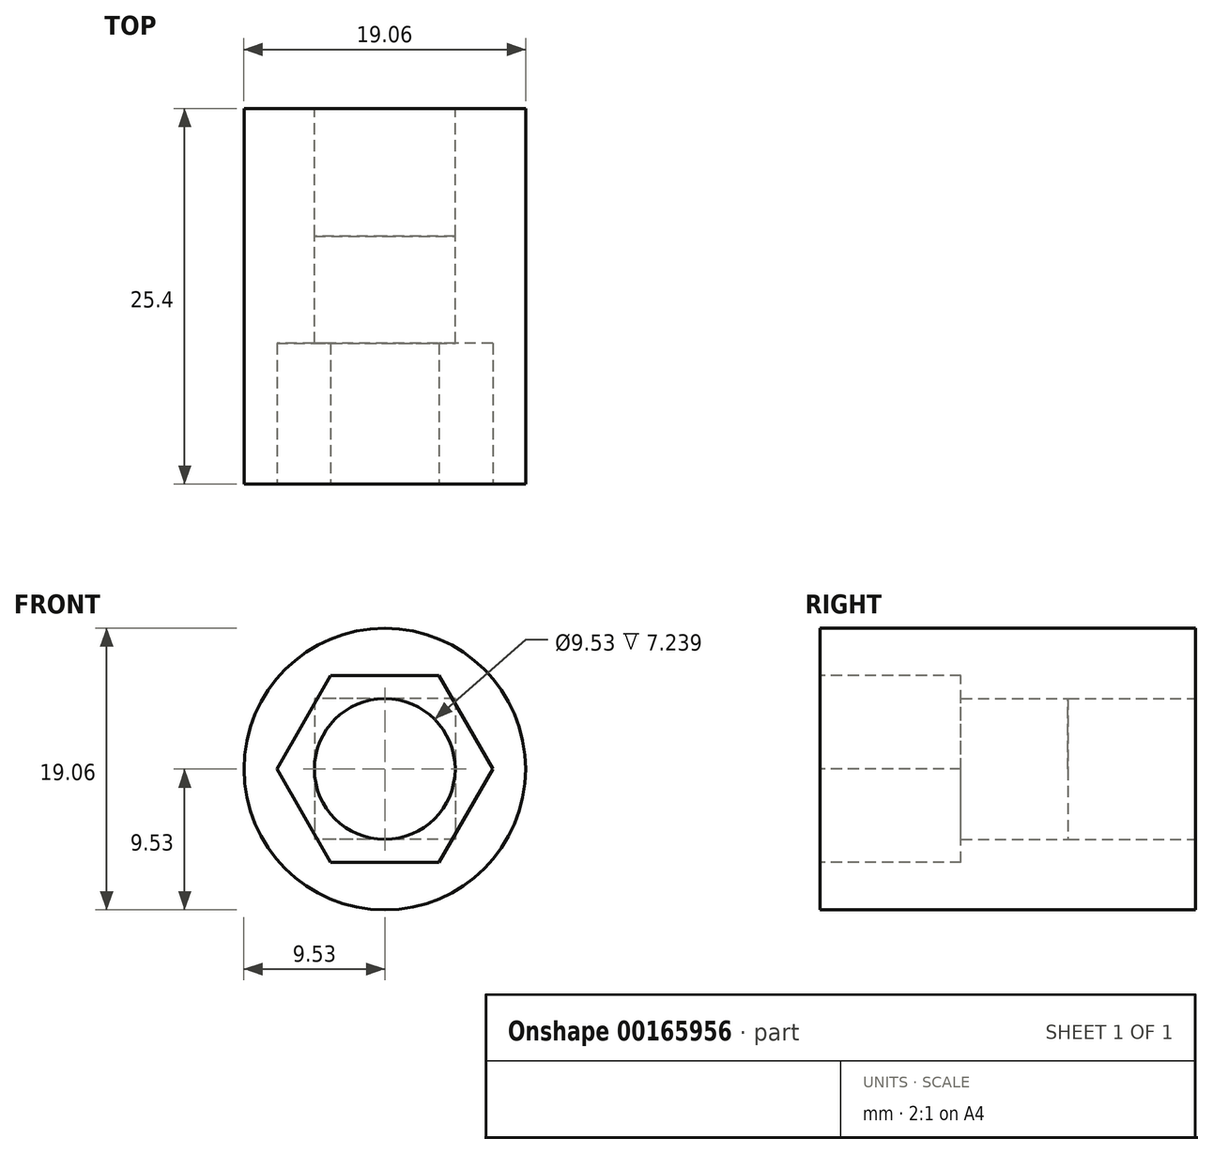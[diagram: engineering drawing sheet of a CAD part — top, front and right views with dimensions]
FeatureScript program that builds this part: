
annotation { "Feature Type Name" : "Feature", "Feature Type Description" : "" }
export const myFeature = defineFeature(function(context is Context, id is Id, definition is map)
    precondition{}
    {
        {
            var Q0;
            Q0=qCreatedBy(makeId("Front.planeOp"),FACE);
            var sketch = newSketch(context, id + "F0", { "sketchPlane" : qUnion([Q0])});
            skCircle(sketch, "E0", {"center": v(0, 0) * mm, "radius": 9.53 * mm});
            skSolve(sketch);
        }
        {
            var Q0;
            Q0 = qSketchRegion(id + "F0", true);
            extrude(context, id + "F1", {"entities" : qUnion([Q0]), "depth" : 25.4 * mm});
        }
        {
            var Q0;
            Q0=qCreatedBy(makeId("Front.planeOp"),FACE);
            var sketch = newSketch(context, id + "F2", { "sketchPlane" : qUnion([Q0])});
            skLineSegment(sketch, "E1.bottom", {"start": v(4.76, 4.76) * mm, "end": v(-4.76, 4.76) * mm});
            skLineSegment(sketch, "E1.top", {"start": v(4.76, -4.76) * mm, "end": v(-4.76, -4.76) * mm});
            skLineSegment(sketch, "E1.left", {"start": v(4.76, 4.76) * mm, "end": v(4.76, -4.76) * mm});
            skLineSegment(sketch, "E1.right", {"start": v(-4.76, 4.76) * mm, "end": v(-4.76, -4.76) * mm});
            skPoint(sketch, "E1.middle", {"position": v(0, 0) * mm});
            skPoint(sketch, "E2.middle", {"position": v(-4.76, 1.68) * mm});
            skCircle(sketch, "E3", {"center": v(0, 0) * mm, "radius": 4.76 * mm});
            skSolve(sketch);
        }
        {
            var Q0;
            {var subQ0=sQuery(id+"F2.wireOp",EDGE,"E3");var subQ1=makeQuery(id+"F2.imprint","INTERSECT",VERTEX,{"derivedFrom":[sQuery(id+"F2.wireOp",EDGE,"E1.bottom"),subQ0]});Q0=makeQuery(id+"F2.imprint","IMPRINT",FACE,{"disambiguationData":[TD([[makeQuery(id+"F2.imprint","IMPRINT",EDGE,{"disambiguationData":[TD([[subQ1,1.0]])],"derivedFrom":subQ0}),1.0]])]});}
            extrude(context, id + "F3", {"entities" : qUnion([Q0]), "operationType" : NewBodyOperationType.REMOVE, "endBound" : BoundingType.THROUGH_ALL, "depth" : 25.4 * mm});
        }
        {
            var Q0;
            {var subQ0=sQuery(id+"F2.wireOp",EDGE,"E1.right");var subQ1=sQuery(id+"F2.wireOp",EDGE,"E1.bottom");var subQ2=makeQuery(id+"F2.imprint","INTERSECT",VERTEX,{"derivedFrom":[subQ1,subQ0]});Q0=makeQuery(id+"F2.imprint","IMPRINT",FACE,{"disambiguationData":[TD([[makeQuery(id+"F2.imprint","IMPRINT",EDGE,{"disambiguationData":[TD([[subQ2,1.0]])],"derivedFrom":subQ1}),1.0]])]});}
            var Q1;
            {var subQ0=sQuery(id+"F2.wireOp",EDGE,"E1.left");var subQ1=sQuery(id+"F2.wireOp",EDGE,"E1.bottom");var subQ2=makeQuery(id+"F2.imprint","INTERSECT",VERTEX,{"derivedFrom":[subQ1,subQ0]});Q1=makeQuery(id+"F2.imprint","IMPRINT",FACE,{"disambiguationData":[TD([[makeQuery(id+"F2.imprint","IMPRINT",EDGE,{"disambiguationData":[TD([[subQ2,-1.0]])],"derivedFrom":subQ1}),1.0]])]});}
            var Q2;
            {var subQ0=sQuery(id+"F2.wireOp",EDGE,"E1.right");var subQ1=sQuery(id+"F2.wireOp",EDGE,"E1.top");var subQ2=makeQuery(id+"F2.imprint","INTERSECT",VERTEX,{"derivedFrom":[subQ1,subQ0]});Q2=makeQuery(id+"F2.imprint","IMPRINT",FACE,{"disambiguationData":[TD([[makeQuery(id+"F2.imprint","IMPRINT",EDGE,{"disambiguationData":[TD([[subQ2,1.0]])],"derivedFrom":subQ1}),-1.0]])]});}
            var Q3;
            {var subQ0=sQuery(id+"F2.wireOp",EDGE,"E1.left");var subQ1=sQuery(id+"F2.wireOp",EDGE,"E1.top");var subQ2=makeQuery(id+"F2.imprint","INTERSECT",VERTEX,{"derivedFrom":[subQ1,subQ0]});Q3=makeQuery(id+"F2.imprint","IMPRINT",FACE,{"disambiguationData":[TD([[makeQuery(id+"F2.imprint","IMPRINT",EDGE,{"disambiguationData":[TD([[subQ2,-1.0]])],"derivedFrom":subQ1}),-1.0]])]});}
            extrude(context, id + "F4", {"entities" : qUnion([Q0, Q1, Q2, Q3]), "operationType" : NewBodyOperationType.REMOVE, "depth" : 8.64 * mm});
        }
        {
            var Q0;
            Q0=makeQuery(id+"F1.opExtrude","CAP_FACE",FACE,{"disambiguationData":[OSD([sQuery(id+"F0.wireOp",EDGE,"E0")])],"isStart":false});
            var sketch = newSketch(context, id + "F5", { "sketchPlane" : qUnion([Q0])});
            skCircle(sketch, "E4.cCircle", {"center": v(0, 0) * mm, "radius": 6.32 * mm, "construction": true});
            skLineSegment(sketch, "E4.0", {"start": v(-3.65, 6.32) * mm, "end": v(3.65, 6.32) * mm});
            skLineSegment(sketch, "E4.1", {"start": v(3.65, 6.32) * mm, "end": v(7.3, 0) * mm});
            skLineSegment(sketch, "E4.2", {"start": v(7.3, 0) * mm, "end": v(3.65, -6.32) * mm});
            skLineSegment(sketch, "E4.3", {"start": v(3.65, -6.32) * mm, "end": v(-3.65, -6.32) * mm});
            skLineSegment(sketch, "E4.4", {"start": v(-3.65, -6.32) * mm, "end": v(-7.3, 0) * mm});
            skLineSegment(sketch, "E4.5", {"start": v(-7.3, 0) * mm, "end": v(-3.65, 6.32) * mm});
            skPoint(sketch, "E4.0.midPoint", {"position": v(0, 6.32) * mm});
            skSolve(sketch);
        }
        {
            var Q0;
            Q0 = qSketchRegion(id + "F5", true);
            extrude(context, id + "F6", {"entities" : qUnion([Q0]), "operationType" : NewBodyOperationType.REMOVE, "oppositeDirection" : true, "depth" : 9.52 * mm});
        }
    });
